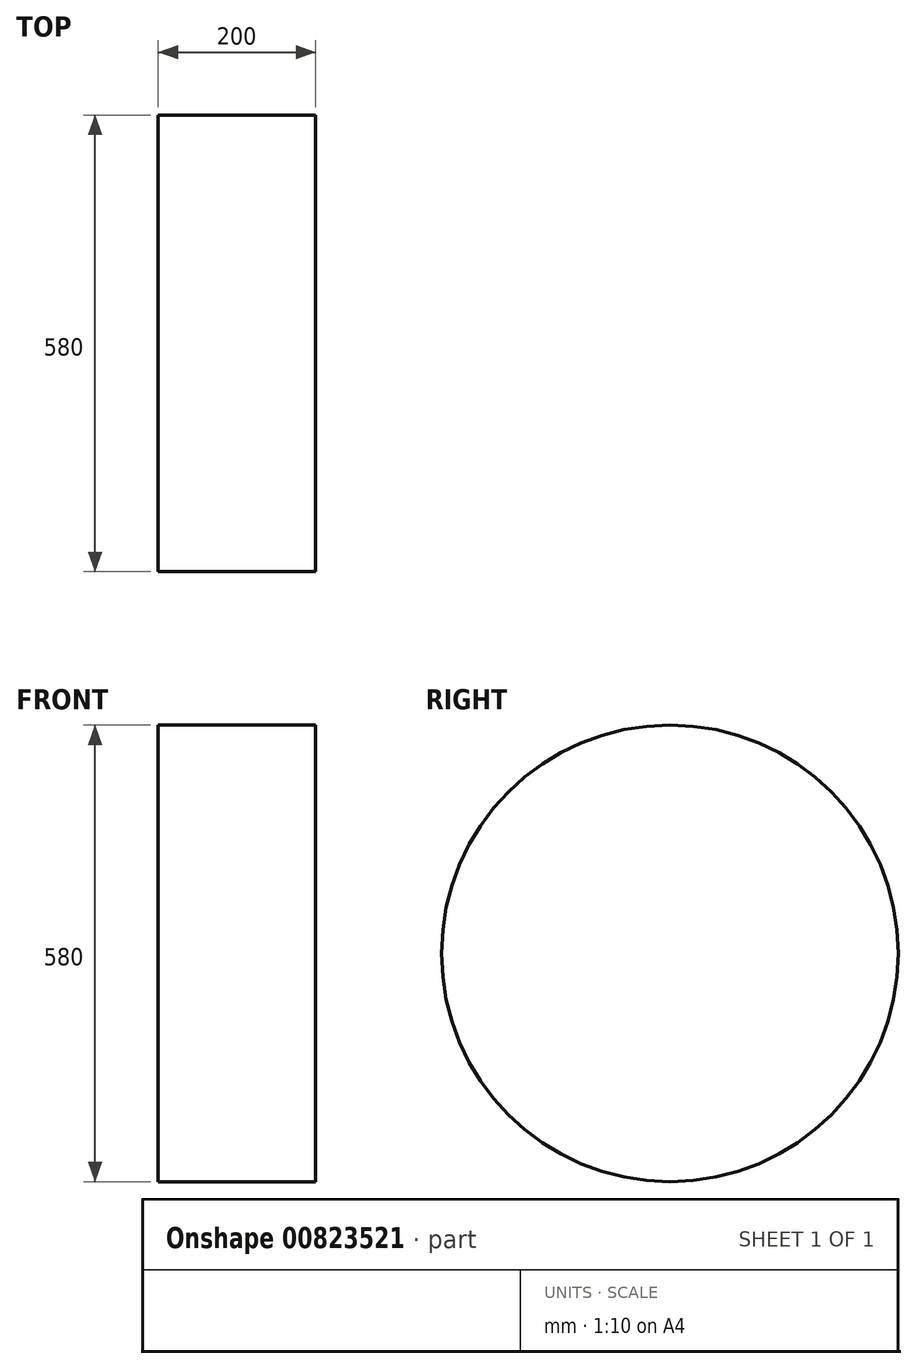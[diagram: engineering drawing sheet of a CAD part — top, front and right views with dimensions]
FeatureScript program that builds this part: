
annotation { "Feature Type Name" : "Feature", "Feature Type Description" : "" }
export const myFeature = defineFeature(function(context is Context, id is Id, definition is map)
    precondition{}
    {
        {
            var Q0;
            Q0=qCreatedBy(makeId("Right.planeOp"),FACE);
            var sketch = newSketch(context, id + "F0", { "sketchPlane" : qUnion([Q0])});
            skCircle(sketch, "E0", {"center": v(0, 0) * mm, "radius": 290 * mm});
            skSolve(sketch);
        }
        {
            var Q0;
            Q0 = qSketchRegion(id + "F0", true);
            extrude(context, id + "F1", {"entities" : qUnion([Q0]), "depth" : 200 * mm, "offsetDistance" : 25 * mm});
        }
    });
